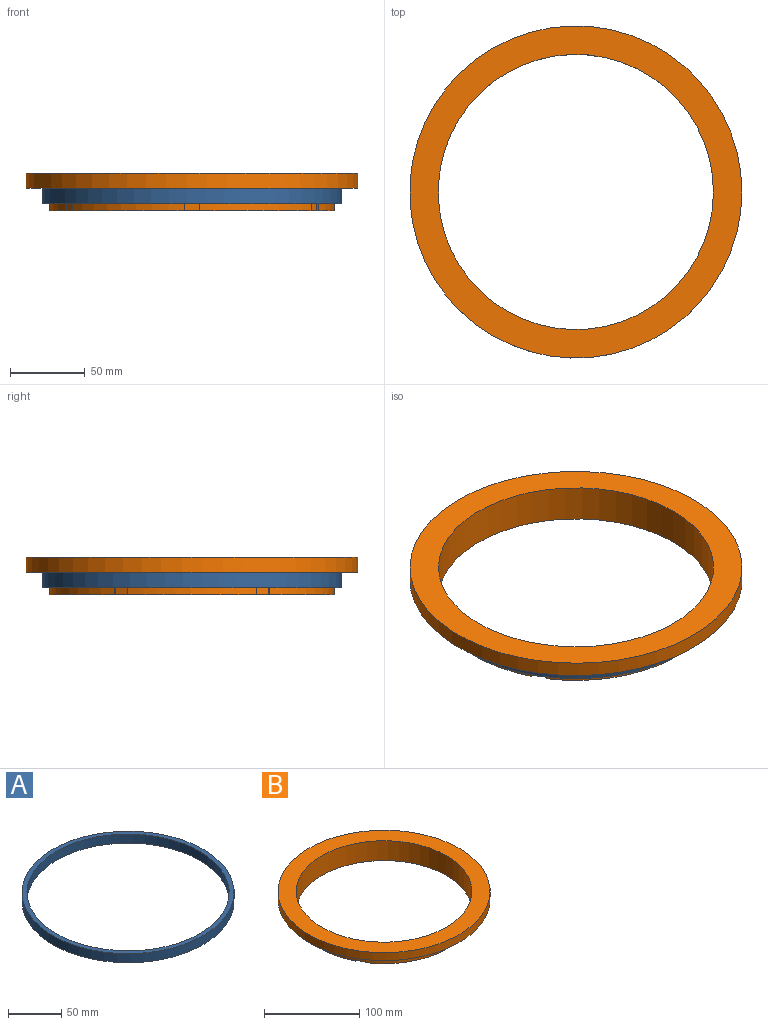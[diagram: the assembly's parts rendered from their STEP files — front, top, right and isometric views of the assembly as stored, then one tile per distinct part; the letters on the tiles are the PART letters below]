
ASSEMBLY  parts=2 mates=1
PART A: 4 faces, bbox 199.7x199.7x10.4 mm
  f0: cylinder r=95.2mm len=190.4mm, axis (0,0,1), area 6229.2mm2, adj f2,f3
  f1: cylinder r=99.85mm len=199.7mm, axis (0,0,1), area 6533.3mm2, adj f2,f3
  f2: plane 199.7x199.7mm, normal (0,0,-1), area 2848.2mm2, adj f0,f1
  f3: plane 199.7x199.7mm, normal (0,0,1), area 2848.2mm2, adj f0,f1
PART B: 30 faces, bbox 222.3x222.3x25.4 mm
  f0: plane 10.67x1.27mm, normal (-0.5,0.87,0), area 15.6mm2, adj f2,f3,f20,f25
  f1: plane 10.67x1.27mm, normal (0.5,-0.87,0), area 15.6mm2, adj f2,f3,f20,f25
  f2: plane 10.67x8.8mm, normal (-0.87,-0.5,0), area 108.4mm2, adj f0,f1,f3,f25
  f3: plane 9.53x6.35mm, normal (0,0,-1), area 15.8mm2, adj f0,f1,f2,f20
  f4: plane 10.67x1.27mm, normal (0.5,0.87,0), area 15.6mm2, adj f6,f7,f20,f25
  f5: plane 10.67x1.27mm, normal (-0.5,-0.87,0), area 15.6mm2, adj f6,f7,f20,f25
  f6: plane 10.67x8.8mm, normal (-0.87,0.5,0), area 108.4mm2, adj f4,f5,f7,f25
  f7: plane 9.53x6.35mm, normal (0,0,-1), area 15.8mm2, adj f4,f5,f6,f20
  f8: plane 10.67x1.47mm, normal (1,0,0), area 15.6mm2, adj f10,f11,f20,f25
  f9: plane 10.67x1.47mm, normal (-1,0,0), area 15.6mm2, adj f10,f11,f20,f25
  f10: plane 10.67x10.16mm, normal (0,1,0), area 108.4mm2, adj f8,f9,f11,f25
  f11: plane 10.16x1.6mm, normal (0,0,-1), area 15.8mm2, adj f8,f9,f10,f20
  f12: plane 10.67x1.27mm, normal (0.5,-0.87,0), area 15.6mm2, adj f14,f15,f20,f25
  f13: plane 10.67x1.27mm, normal (-0.5,0.87,0), area 15.6mm2, adj f14,f15,f20,f25
  f14: plane 10.67x8.8mm, normal (0.87,0.5,0), area 108.4mm2, adj f12,f13,f15,f25
  f15: plane 9.53x6.35mm, normal (0,0,-1), area 15.8mm2, adj f12,f13,f14,f20
  f16: plane 10.67x1.27mm, normal (-0.5,-0.87,0), area 15.6mm2, adj f18,f19,f20,f25
  f17: plane 10.67x1.27mm, normal (0.5,0.87,0), area 15.6mm2, adj f18,f19,f20,f25
  f18: plane 10.67x8.8mm, normal (0.87,-0.5,0), area 108.4mm2, adj f16,f17,f19,f25
  f19: plane 9.53x6.35mm, normal (0,0,-1), area 15.8mm2, adj f16,f17,f18,f20
  f20: cylinder r=95.2mm len=190.4mm, axis (0,0,1), area 8465.2mm2, adj f0,f1,f3,f4,f5,f7,f8,f9
  f21: cylinder r=111.12mm len=222.25mm, axis (0,0,-1), area 7093.9mm2, adj f22,f23
  f22: plane 222.25x222.25mm, normal (0,0,1), area 12161mm2, adj f21,f24
  f23: plane 222.25x222.25mm, normal (0,0,-1), area 10322.9mm2, adj f20,f21
  f24: cylinder r=92.08mm len=184.15mm, axis (0,0,1), area 14694.5mm2, adj f22,f25
  f25: plane 190.4x190.13mm, normal (0,0,-1), area 1743.2mm2, adj f0,f1,f2,f4,f5,f6,f8,f9
  f26: plane 10.67x1.47mm, normal (-1,0,0), area 15.6mm2, adj f20,f25,f28,f29
  f27: plane 10.67x1.47mm, normal (1,0,0), area 15.6mm2, adj f20,f25,f28,f29
  f28: plane 10.67x10.16mm, normal (0,-1,0), area 108.4mm2, adj f25,f26,f27,f29
  f29: plane 10.16x1.6mm, normal (0,0,-1), area 15.8mm2, adj f20,f26,f27,f28
PLACE A t=(0.45,-0.05,2.07)mm
PLACE B t=(0.45,-0.05,2.07)mm
MATE parallel A.f1 <-> B.f21  axis (0,0,1) through (0.45,-0.05,2.07)mm
